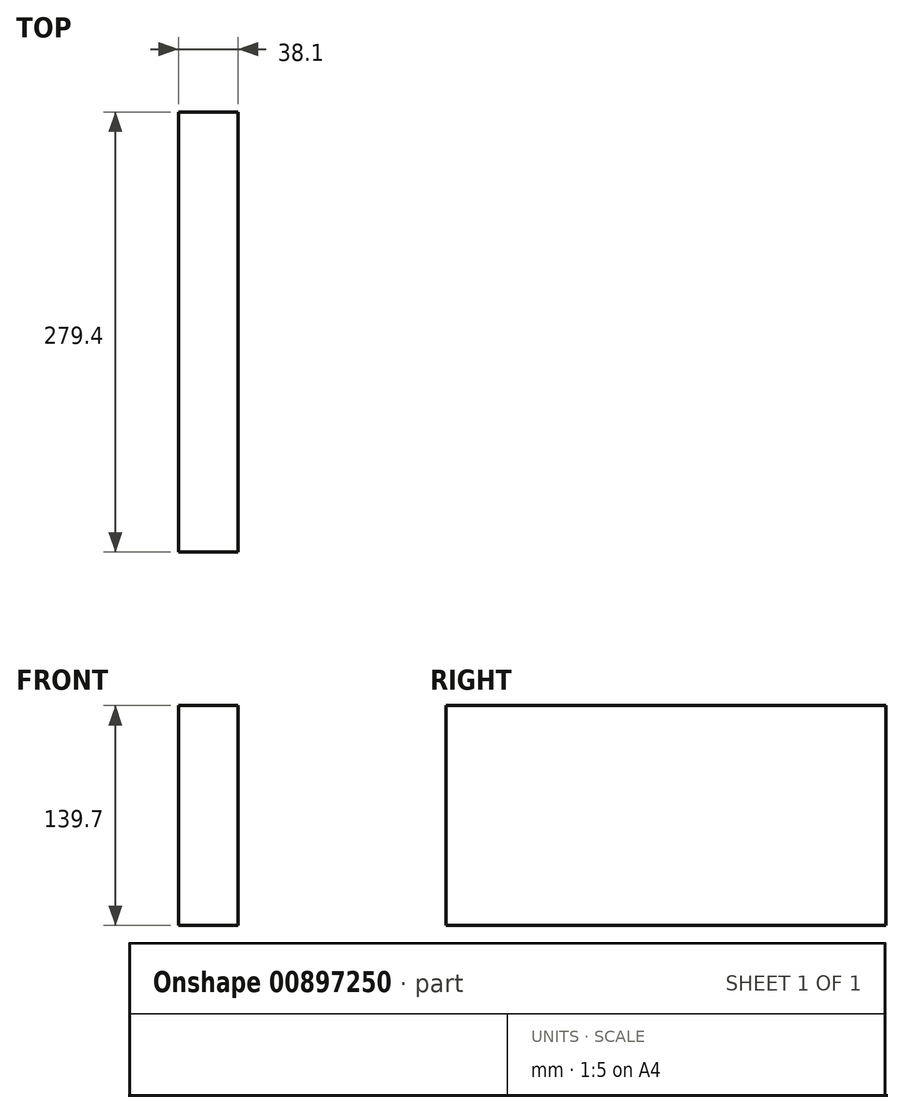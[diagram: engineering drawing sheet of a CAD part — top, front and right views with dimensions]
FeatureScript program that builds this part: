
annotation { "Feature Type Name" : "Feature", "Feature Type Description" : "" }
export const myFeature = defineFeature(function(context is Context, id is Id, definition is map)
    precondition{}
    {
        {
            var Q0;
            Q0=qCreatedBy(makeId("Front.planeOp"),FACE);
            var sketch = newSketch(context, id + "F0", { "sketchPlane" : qUnion([Q0])});
            skLineSegment(sketch, "E0.bottom", {"start": v(-19.05, 69.85) * mm, "end": v(19.05, 69.85) * mm});
            skLineSegment(sketch, "E0.top", {"start": v(-19.05, -69.85) * mm, "end": v(19.05, -69.85) * mm});
            skLineSegment(sketch, "E0.left", {"start": v(-19.05, 69.85) * mm, "end": v(-19.05, -69.85) * mm});
            skLineSegment(sketch, "E0.right", {"start": v(19.05, 69.85) * mm, "end": v(19.05, -69.85) * mm});
            skPoint(sketch, "E0.middle", {"position": v(0, 0) * mm});
            skSolve(sketch);
        }
        {
            var Q0;
            Q0=makeQuery(id+"F0.imprint","IMPRINT",FACE,{"disambiguationData":[TD([[makeQuery(id+"F0.imprint","IMPRINT",EDGE,{"derivedFrom":sQuery(id+"F0.wireOp",EDGE,"E0.bottom")}),-1.0]])]});
            extrude(context, id + "F1", {"entities" : qUnion([Q0]), "depth" : 279.4 * mm, "offsetDistance" : 25.4 * mm});
        }
    });
